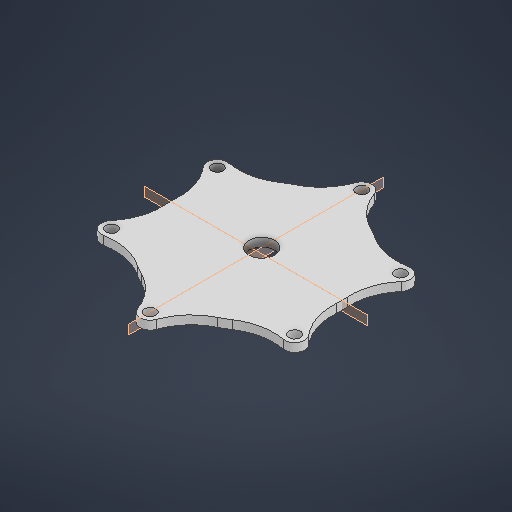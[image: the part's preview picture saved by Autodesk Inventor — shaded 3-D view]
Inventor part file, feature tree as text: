
AUTODESK INVENTOR PART (.ipt)
format: ipt  version: 2025.3 (Build 293356000, 356)  size: 258,560 bytes
history: native  units: mm
features: sketch x3, extrude x3
ambient origin geometry x8: Origin, YZ Plane, XZ Plane, XY Plane, X Axis, Y Axis, Z Axis, Center Point
bodies: Body1 (feature_tree)
feature tree (6):
  sketch  "Sketch1"  dims[d16=60.0mm d17=55.0mm]
  extrude  "Extrusion5"  Depth=55.0mm
  extrude  "Extrusion6"  Depth=37.0mm
  extrude  "Extrusion12"  Depth=2.0mm
  sketch  "Sketch Circular Pattern1"  dims[d18=7.0mm d19=37.0mm]
  sketch  "Sketch10"  dims[d21=20.0mm d22=4.0mm d23=60.0mm d25=360.0deg d27=3.0mm d28=0.0mm d29=3.0mm d30=0.0mm d58=9.0mm d59=45.0mm d60=2.0mm d61=20.25mm d62=0.0mm d3=0.5mm d4=0.872665mm d5=0.5mm d6=0.872665mm d39=0.5mm d40=0.872665mm d41=0.5mm d42=0.872665mm]
